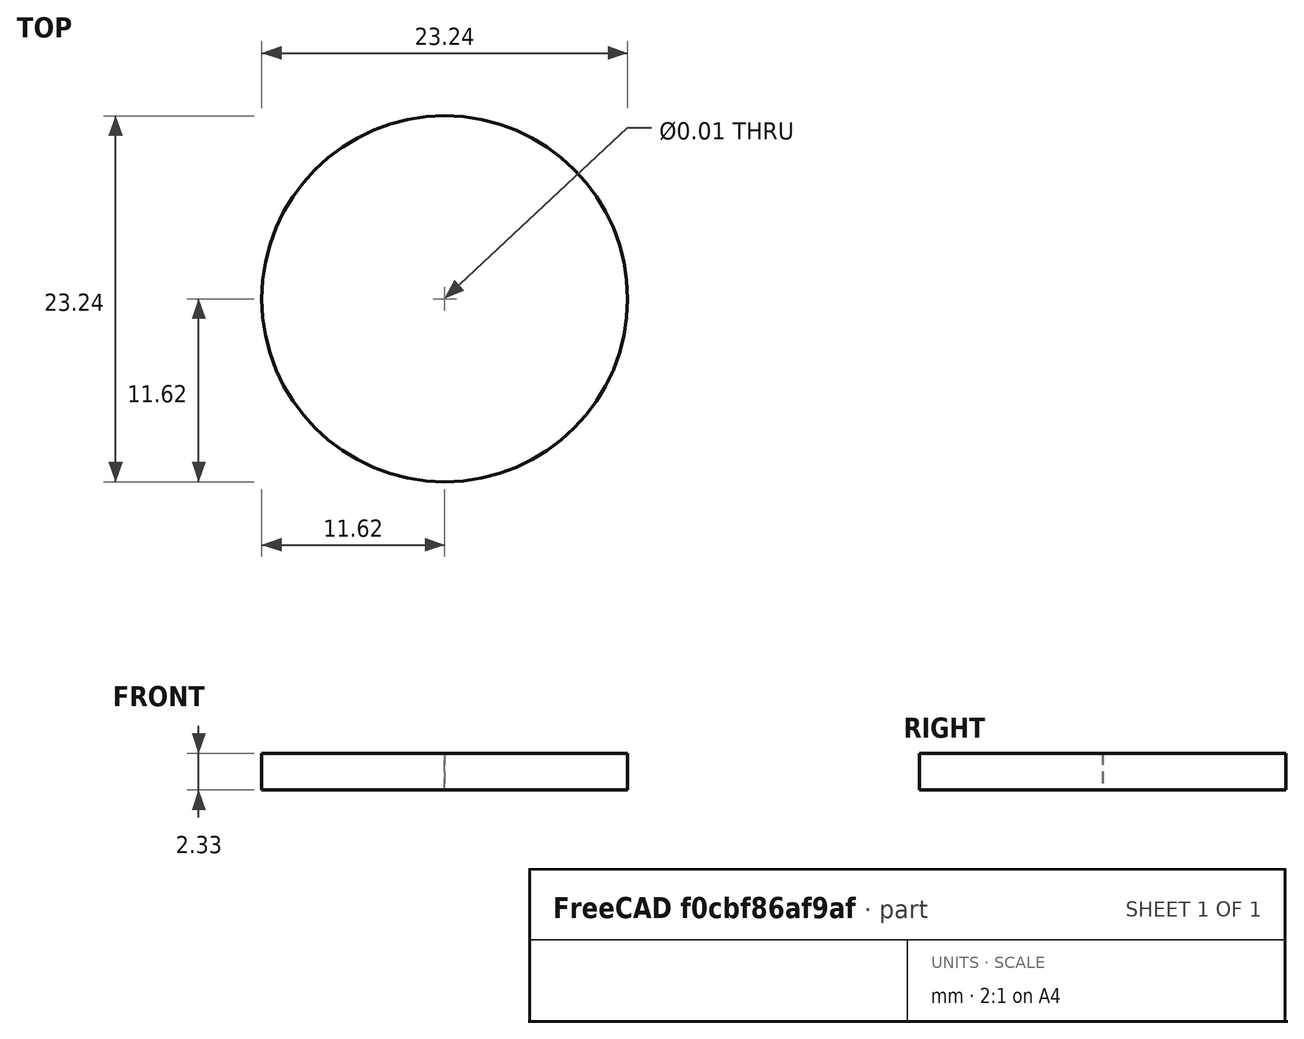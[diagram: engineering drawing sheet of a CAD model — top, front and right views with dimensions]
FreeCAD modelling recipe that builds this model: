
FCSTD DOCUMENT  (FreeCAD 1.0R39109 (Git))
Label: Tube
License: All rights reserved
LicenseURL: http://en.wikipedia.org/wiki/All_rights_reserved
objects: Sketcher::SketchObject×1, Spreadsheet::Sheet×1, PartDesign::Pad×1, PartDesign::Body×1
note: 6 computed .brp shape members not serialized (recipe doc carries the construction recipe); baked Part::Feature solids carry a one-line shape summary decoded from their .brp

FEATURE [Sketcher::SketchObject] Sketch
  ArcFitTolerance = 1e-06
  AttachmentSupport = -> [XY_Plane]
  FullyConstrained = true
  MakeInternals = false
  MapMode = 5
  expr: Constraints[2] = Spreadsheet.inner_diameter
  expr: Constraints[3] = Spreadsheet.outer_diameter
  sketch-geometry (2):
    g0: Circle CenterX=0 CenterY=0 CenterZ=0 NormalX=0 NormalY=0 NormalZ=1 AngleXU=0 Radius=11.625
    g1: Circle CenterX=0 CenterY=0 CenterZ=0 NormalX=0 NormalY=0 NormalZ=1 AngleXU=0 Radius=0.005
  constraints (4):
    c: Coincident(g0,g-1)
    c: Coincident(g1,g0)
    c: Diameter(g1) = 0.01
    c: Diameter(g0) = 23.25
FEATURE [Spreadsheet::Sheet] Spreadsheet
  cells = A1='inner_diameter; B1(inner_diameter)=0.01; A2='outer_diameter; B2(outer_diameter)=23.25; A3='length; B3(length)=2.33
FEATURE [PartDesign::Pad] Pad
  Direction = (0,0,1)
  Length = 2.33
  Length2 = 10
  Profile = -> Sketch
  ReferenceAxis = -> Sketch [N_Axis]
  Suppressed = false
  Type = 0
  expr: Length = Spreadsheet.length
FEATURE [PartDesign::Body] Body
  AllowCompound = false
  Group = -> [Sketch,Pad]
  Origin = -> Origin
  Tip = -> Pad
